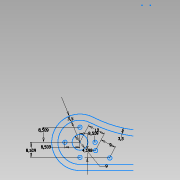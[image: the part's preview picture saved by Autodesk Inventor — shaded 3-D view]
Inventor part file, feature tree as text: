
AUTODESK INVENTOR PART (.ipt)
format: ipt  version: 2015 SP1 (Build 190203100, 203)  size: 78,336 bytes
history: native  units: mm
features: sketch x1
ambient origin geometry x8: Origin, YZ Plane, XZ Plane, XY Plane, X Axis, Y Axis, Z Axis, Center Point
feature tree (1):
  sketch  "Sketch1"  dims[d47=8.509mm d48=8.509mm d49=8.509mm d50=8.509mm d51=10.0mm d53=9.0mm d56=9.0mm d58=4.19811mm d67=3.5mm d68=3.5mm]
